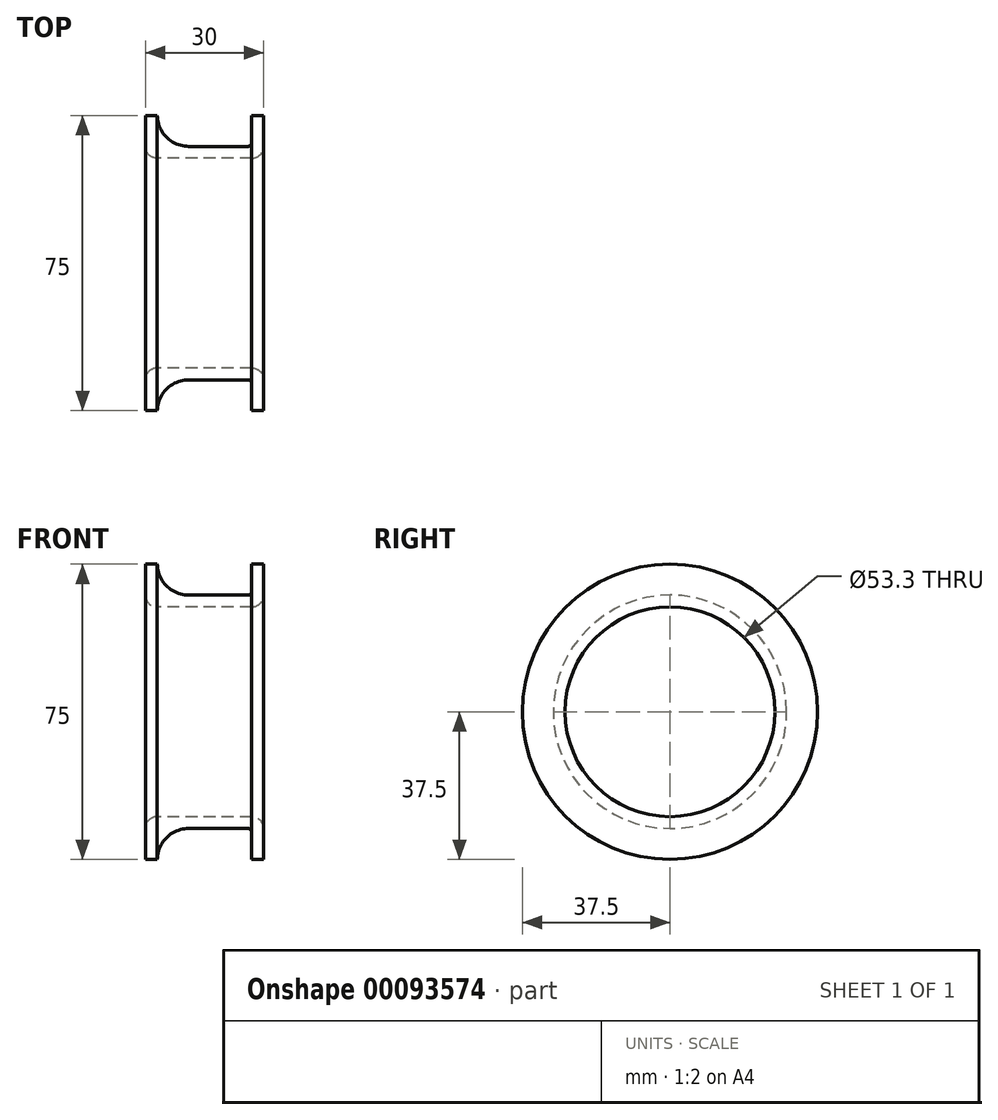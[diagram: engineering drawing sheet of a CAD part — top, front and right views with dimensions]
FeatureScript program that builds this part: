
annotation { "Feature Type Name" : "Feature", "Feature Type Description" : "" }
export const myFeature = defineFeature(function(context is Context, id is Id, definition is map)
    precondition{}
    {
        {
            var Q0;
            Q0=qCreatedBy(makeId("Top.planeOp"),FACE);
            var sketch = newSketch(context, id + "F0", { "sketchPlane" : qUnion([Q0])});
            skLineSegment(sketch, "E0", {"start": v(-38.03, 0) * mm, "end": v(48.17, 0) * mm, "construction": true});
            skLineSegment(sketch, "E1", {"start": v(0, 26.65) * mm, "end": v(-30, 26.65) * mm});
            skLineSegment(sketch, "E2", {"start": v(-30, 26.65) * mm, "end": v(-30, 37.5) * mm});
            skLineSegment(sketch, "E3", {"start": v(-30, 37.5) * mm, "end": v(-27, 37.5) * mm});
            skLineSegment(sketch, "E4", {"start": v(-27, 37.5) * mm, "end": v(-27, 29.65) * mm});
            skLineSegment(sketch, "E5", {"start": v(-27, 29.65) * mm, "end": v(-3, 29.65) * mm});
            skLineSegment(sketch, "E6", {"start": v(-3, 29.65) * mm, "end": v(-3, 37.5) * mm});
            skLineSegment(sketch, "E7", {"start": v(-3, 37.5) * mm, "end": v(0, 37.5) * mm});
            skLineSegment(sketch, "E8", {"start": v(0, 37.5) * mm, "end": v(0, 26.65) * mm});
            skSolve(sketch);
        }
        {
            var Q0;
            Q0 = qSketchRegion(id + "F0", true);
            var Q1;
            Q1=sQuery(id+"F0.wireOp",EDGE,"E0");
            revolve(context, id + "F1", {"entities" : qUnion([Q0]), "axis" : qUnion([Q1]), "revolveType" : RevolveType.FULL});
        }
        {
            var Q0;
            Q0=makeQuery(id+"F1.opRevolve","SWEPT_EDGE",EDGE,{"disambiguationData":[OSD([sQuery(id+"F0.wireOp",EDGE,"E4"),sQuery(id+"F0.wireOp",EDGE,"E5")])]});
            fillet(context, id + "F2", {"entities" : qUnion([Q0]), "radius" : 8 * mm, "tangentPropagation" : true, "allowEdgeOverflow" : false});
        }
        {
            var Q0;
            Q0=makeQuery(id+"F1.opRevolve","SWEPT_EDGE",EDGE,{"disambiguationData":[OSD([sQuery(id+"F0.wireOp",EDGE,"E1"),sQuery(id+"F0.wireOp",EDGE,"E8")])]});
            var Q1;
            Q1=makeQuery(id+"F1.opRevolve","SWEPT_EDGE",EDGE,{"disambiguationData":[OSD([sQuery(id+"F0.wireOp",EDGE,"E1"),sQuery(id+"F0.wireOp",EDGE,"E2")])]});
            fillet(context, id + "F3", {"entities" : qUnion([Q0, Q1]), "radius" : 3 * mm, "tangentPropagation" : true, "allowEdgeOverflow" : false});
        }
        {
            var Q0;
            Q0=makeQuery(id+"F1.opRevolve","SWEPT_EDGE",EDGE,{"disambiguationData":[OSD([sQuery(id+"F0.wireOp",EDGE,"E5"),sQuery(id+"F0.wireOp",EDGE,"E6")])]});
            fillet(context, id + "F4", {"entities" : qUnion([Q0]), "radius" : 1 * mm, "tangentPropagation" : true, "allowEdgeOverflow" : false});
        }
    });
